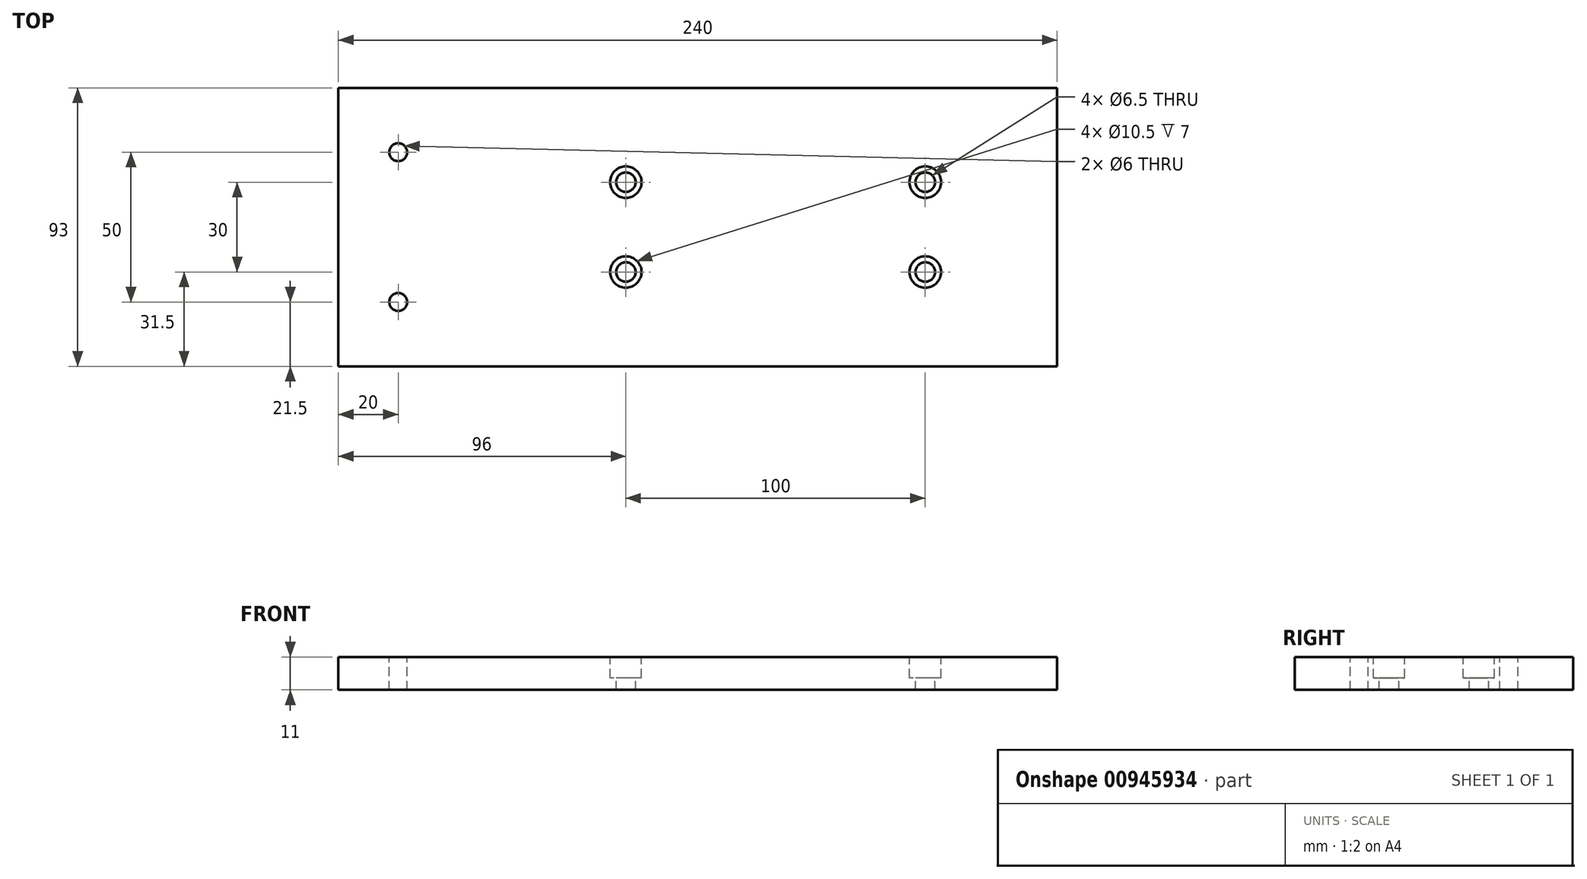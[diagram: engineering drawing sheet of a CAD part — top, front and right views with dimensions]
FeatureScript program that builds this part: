
annotation { "Feature Type Name" : "Feature", "Feature Type Description" : "" }
export const myFeature = defineFeature(function(context is Context, id is Id, definition is map)
    precondition{}
    {
        {
            var Q0;
            Q0=qCreatedBy(makeId("Top.planeOp"),FACE);
            var sketch = newSketch(context, id + "F0", { "sketchPlane" : qUnion([Q0])});
            skLineSegment(sketch, "E0.bottom", {"start": v(120, -46.5) * mm, "end": v(-120, -46.5) * mm});
            skLineSegment(sketch, "E0.top", {"start": v(120, 46.5) * mm, "end": v(-120, 46.5) * mm});
            skLineSegment(sketch, "E0.left", {"start": v(120, -46.5) * mm, "end": v(120, 46.5) * mm});
            skLineSegment(sketch, "E0.right", {"start": v(-120, -46.5) * mm, "end": v(-120, 46.5) * mm});
            skPoint(sketch, "E0.middle", {"position": v(0, 0) * mm});
            skSolve(sketch);
        }
        {
            var Q0;
            Q0 = qSketchRegion(id + "F0", true);
            extrude(context, id + "F1", {"entities" : qUnion([Q0]), "depth" : 11 * mm, "offsetDistance" : 25 * mm});
        }
        {
            var Q0;
            Q0=makeQuery(id+"F1.opExtrude","CAP_FACE",FACE,{"disambiguationData":[OSD([sQuery(id+"F0.wireOp",EDGE,"E0.bottom"),sQuery(id+"F0.wireOp",EDGE,"E0.top"),sQuery(id+"F0.wireOp",EDGE,"E0.left"),sQuery(id+"F0.wireOp",EDGE,"E0.right")])],"isStart":false});
            var sketch = newSketch(context, id + "F2", { "sketchPlane" : qUnion([Q0])});
            skCircle(sketch, "E1", {"center": v(76, 15) * mm, "radius": 3.25 * mm});
            skCircle(sketch, "E2", {"center": v(-24, 15) * mm, "radius": 3.25 * mm});
            skCircle(sketch, "E3", {"center": v(-100, 25) * mm, "radius": 3 * mm});
            skLineSegment(sketch, "E4", {"start": v(-120, 0) * mm, "end": v(120, 0) * mm, "construction": true});
            skCircle(sketch, "E5.MirrorC", {"center": v(-100, -25) * mm, "radius": 3 * mm});
            skCircle(sketch, "E6.MirrorC", {"center": v(-24, -15) * mm, "radius": 3.25 * mm});
            skCircle(sketch, "E7.MirrorC", {"center": v(76, -15) * mm, "radius": 3.25 * mm});
            skSolve(sketch);
        }
        {
            var Q0;
            Q0 = qSketchRegion(id + "F2", true);
            extrude(context, id + "F3", {"entities" : qUnion([Q0]), "operationType" : NewBodyOperationType.REMOVE, "endBound" : BoundingType.THROUGH_ALL, "oppositeDirection" : true, "depth" : 25 * mm, "offsetDistance" : 25 * mm});
        }
        {
            var Q0;
            Q0=makeQuery(id+"F1.opExtrude","CAP_FACE",FACE,{"disambiguationData":[OSD([sQuery(id+"F0.wireOp",EDGE,"E0.bottom"),sQuery(id+"F0.wireOp",EDGE,"E0.top"),sQuery(id+"F0.wireOp",EDGE,"E0.left"),sQuery(id+"F0.wireOp",EDGE,"E0.right")])],"isStart":false});
            var sketch = newSketch(context, id + "F4", { "sketchPlane" : qUnion([Q0])});
            skCircle(sketch, "E8", {"center": v(-24, 15) * mm, "radius": 5.25 * mm});
            skCircle(sketch, "E9", {"center": v(76, 15) * mm, "radius": 5.25 * mm});
            skCircle(sketch, "E10", {"center": v(76, -15) * mm, "radius": 5.25 * mm});
            skCircle(sketch, "E11", {"center": v(-24, -15) * mm, "radius": 5.25 * mm});
            skSolve(sketch);
        }
        {
            var Q0;
            Q0 = qSketchRegion(id + "F4", true);
            extrude(context, id + "F5", {"entities" : qUnion([Q0]), "operationType" : NewBodyOperationType.REMOVE, "oppositeDirection" : true, "depth" : 7 * mm, "offsetDistance" : 25 * mm});
        }
    });
